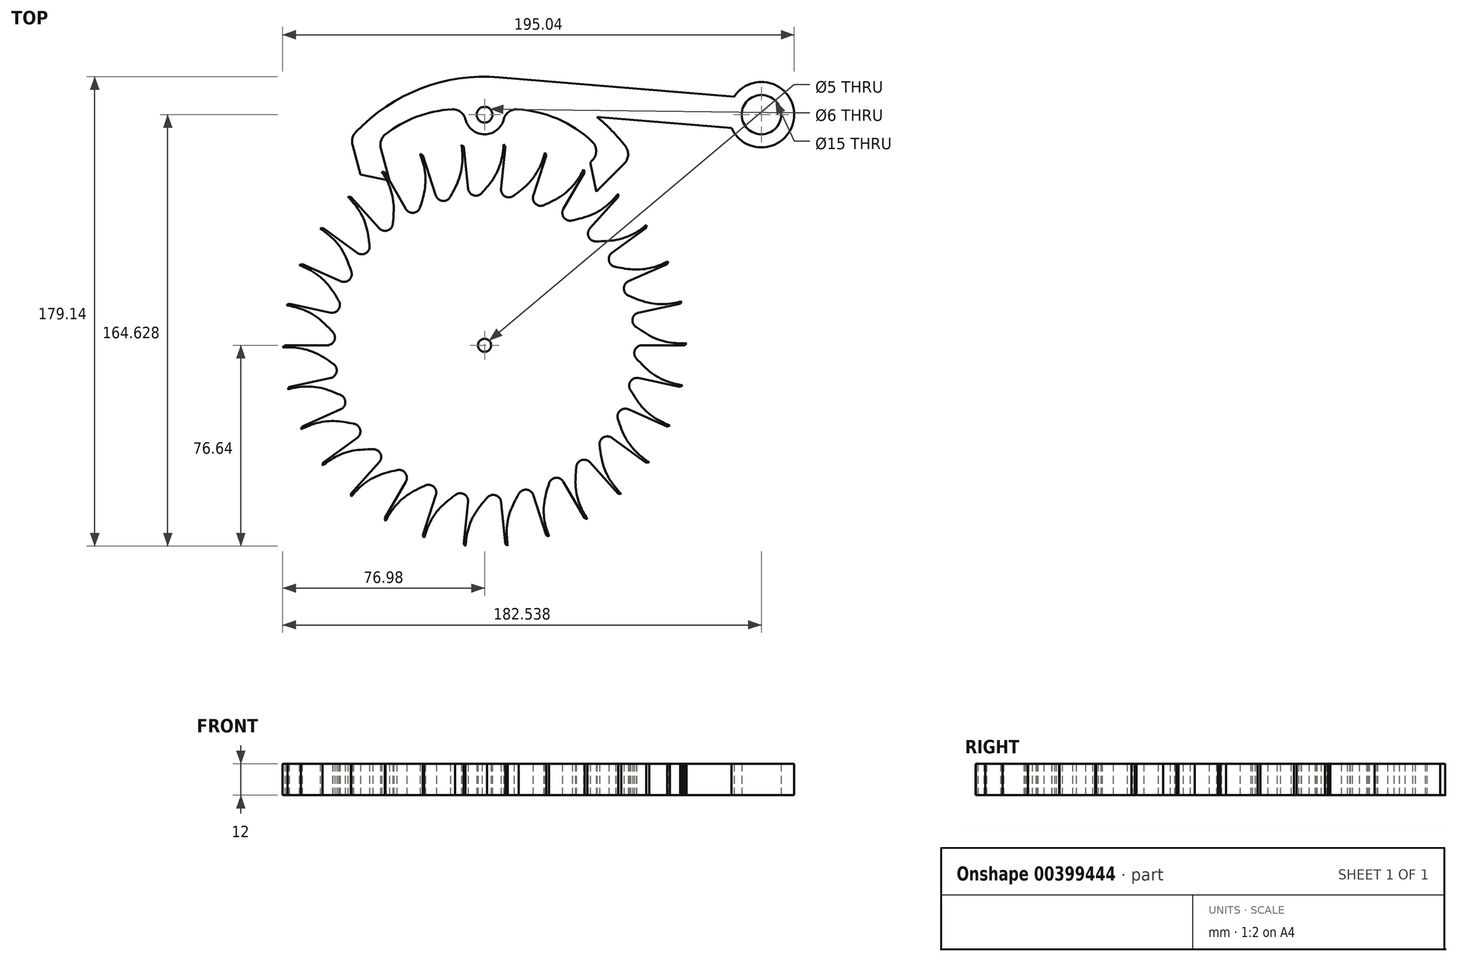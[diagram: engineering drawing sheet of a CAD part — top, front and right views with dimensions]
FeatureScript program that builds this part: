
annotation { "Feature Type Name" : "Feature", "Feature Type Description" : "" }
export const myFeature = defineFeature(function(context is Context, id is Id, definition is map)
    precondition{}
    {
        {
            var Q0;
            Q0=qCreatedBy(makeId("Top.planeOp"),FACE);
            var sketch = newSketch(context, id + "F0", { "sketchPlane" : qUnion([Q0])});
            skCircle(sketch, "E0", {"center": v(0, 0) * mm, "radius": 76.2 * mm, "construction": true});
            skCircle(sketch, "E1", {"center": v(0, 0) * mm, "radius": 95.25 * mm, "construction": true});
            skCircle(sketch, "E2", {"center": v(0, 0) * mm, "radius": 57.15 * mm, "construction": true});
            skLineSegment(sketch, "E3", {"start": v(0, 0) * mm, "end": v(0, 0) * mm});
            skPoint(sketch, "E4.positionSnap0", {"position": v(0, -4366.16) * mm});
            skCircle(sketch, "E5", {"center": v(0, 0) * mm, "radius": 2.5 * mm});
            skLineSegment(sketch, "E6", {"start": v(0, 0) * mm, "end": v(62.62, 108.46) * mm, "construction": true});
            skLineSegment(sketch, "E7", {"start": v(0, 0) * mm, "end": v(-66.51, 115.2) * mm, "construction": true});
            skLineSegment(sketch, "E8", {"start": v(0, 0) * mm, "end": v(-92.02, 102.2) * mm, "construction": true});
            skLineSegment(sketch, "E9", {"start": v(-109.9, 24.54) * mm, "end": v(65, 125.52) * mm, "construction": true});
            skPoint(sketch, "E10", {"position": v(-38.1, 66) * mm});
            skPoint(sketch, "E11", {"position": v(0, 87.99) * mm});
            skLineSegment(sketch, "E12", {"start": v(-101.63, 31.65) * mm, "end": v(76.72, 130.52) * mm, "construction": true});
            skLineSegment(sketch, "E13", {"start": v(-38.1, 66) * mm, "end": v(-39.17, 66.28) * mm});
            skLineSegment(sketch, "E14", {"start": v(-38.1, 66) * mm, "end": v(-28.57, 49.5) * mm});
            skArc(sketch, "E15", {"start": v(-40.2, 44.64) * mm, "mid": v(-36.93, 43.84) * mm, "end": v(-34.97, 46.57) * mm});
            skFitSpline(sketch, "E16", {"points": [v(-39.17, 66.28) * mm, v(-34.97, 46.57) * mm], "startDerivative": vector(5.47, -16.79) * mm, "endDerivative": vector(-0.66, -22.87) * mm});
            skPoint(sketch, "E17", {"position": v(-40.2, 44.64) * mm});
            skSolve(sketch);
        }
        {
            var Q0;
            Q0=qCreatedBy(makeId("Top.planeOp"),FACE);
            var sketch = newSketch(context, id + "F1", { "sketchPlane" : qUnion([Q0])});
            skArc(sketch, "E18.0", {"start": v(-40.2, 44.64) * mm, "mid": v(-36.93, 43.84) * mm, "end": v(-34.97, 46.57) * mm});
            skFitSpline(sketch, "E18.1", {"points": [v(-39.17, 66.28) * mm, v(-36.46, 61.15) * mm, v(-34.75, 54.19) * mm, v(-34.97, 46.57) * mm]});
            skLineSegment(sketch, "E18.2", {"start": v(-38.1, 66) * mm, "end": v(-28.57, 49.5) * mm});
            skLineSegment(sketch, "E19.0", {"start": v(-38.24, 42.47) * mm, "end": v(-40.2, 44.64) * mm});
            skPoint(sketch, "E20.orphan", {"position": v(-92.02, 102.2) * mm});
            skArc(sketch, "E21.0", {"start": v(-38.24, 42.47) * mm, "mid": v(33.6, -46.24) * mm, "end": v(-28.57, 49.5) * mm});
            skCircle(sketch, "E22.1", {"center": v(0, 0) * mm, "radius": 2.5 * mm});
            skLineSegment(sketch, "E23.0", {"start": v(-38.1, 66) * mm, "end": v(-39.17, 66.28) * mm});
            skSolve(sketch);
        }
        {
            var Q0;
            Q0 = qSketchRegion(id + "F1", true);
            extrude(context, id + "F2", {"entities" : qUnion([Q0]), "depth" : 12 * mm});
        }
        {
            var Q0;
            Q0=makeQuery(id+"F2.opExtrude","SWEPT_BODY",BODY,{"disambiguationData":[OSD([sQuery(id+"F1.wireOp",EDGE,"E18.0"),sQuery(id+"F1.wireOp",EDGE,"E18.1"),sQuery(id+"F1.wireOp",EDGE,"E18.2"),sQuery(id+"F1.wireOp",EDGE,"E19.0"),sQuery(id+"F1.wireOp",EDGE,"E21.0"),sQuery(id+"F1.wireOp",EDGE,"E22.1"),sQuery(id+"F1.wireOp",EDGE,"E23.0")])]});
            var Q1;
            Q1=makeQuery(id+"F2.opExtrude","SWEPT_FACE",FACE,{"disambiguationData":[OSD([sQuery(id+"F1.wireOp",EDGE,"E22.1")])]});
            circularPattern(context, id + "F3", {"operationType" : NewBodyOperationType.ADD, "entities" : qUnion([Q0]), "axis" : qUnion([Q1]), "angle" : 360 * degree, "instanceCount" : 30, "equalSpace" : true});
        }
        {
            var Q0;
            Q0=qCreatedBy(makeId("Top.planeOp"),FACE);
            var sketch = newSketch(context, id + "F4", { "sketchPlane" : qUnion([Q0])});
            skLineSegment(sketch, "E24", {"start": v(0, 0) * mm, "end": v(-58.34, 89.84) * mm, "construction": true});
            skLineSegment(sketch, "E25", {"start": v(0, 0) * mm, "end": v(-62.87, 86.53) * mm, "construction": true});
            skLineSegment(sketch, "E26", {"start": v(0, 0) * mm, "end": v(63.2, 97.32) * mm, "construction": true});
            skLineSegment(sketch, "E27", {"start": v(0, 0) * mm, "end": v(67.16, 92.44) * mm, "construction": true});
            skPoint(sketch, "E28", {"position": v(-41.5, 63.9) * mm});
            skPoint(sketch, "E29", {"position": v(41.5, 63.9) * mm});
            skLineSegment(sketch, "E30", {"start": v(-47.33, 65.15) * mm, "end": v(-36.25, 62.8) * mm});
            skLineSegment(sketch, "E31", {"start": v(40.26, 69.74) * mm, "end": v(42.62, 58.66) * mm});
            skLineSegment(sketch, "E32", {"start": v(40.26, 69.74) * mm, "end": v(41.08, 70.56) * mm});
            skLineSegment(sketch, "E33", {"start": v(-36.25, 62.8) * mm, "end": v(-39.58, 75.22) * mm});
            skCircle(sketch, "E34", {"center": v(0, 87.99) * mm, "radius": 3 * mm});
            skArc(sketch, "E35", {"start": v(-7.29, 86.22) * mm, "mid": v(0, 80.49) * mm, "end": v(7.29, 86.22) * mm});
            skArc(sketch, "E36", {"start": v(53.72, 75.88) * mm, "mid": v(3.5, 102.4) * mm, "end": v(-49.19, 81.22) * mm});
            skArc(sketch, "E37.trimOffspring", {"start": v(41, 77.72) * mm, "mid": v(27.8, 86.42) * mm, "end": v(12.41, 90.03) * mm});
            skArc(sketch, "E38.trimOffspring", {"start": v(-12.41, 90.03) * mm, "mid": v(-25.87, 87.2) * mm, "end": v(-37.85, 80.44) * mm});
            skPoint(sketch, "E39.visualSharp", {"position": v(7.22, 90) * mm});
            skArc(sketch, "E39.filletArc", {"start": v(12.41, 90.03) * mm, "mid": v(9.16, 89.05) * mm, "end": v(7.29, 86.22) * mm});
            skPoint(sketch, "E40.visualSharp", {"position": v(-7.22, 90) * mm});
            skArc(sketch, "E40.filletArc", {"start": v(-7.29, 86.22) * mm, "mid": v(-9.16, 89.05) * mm, "end": v(-12.41, 90.03) * mm});
            skLineSegment(sketch, "E41", {"start": v(-47.33, 65.15) * mm, "end": v(-50.38, 76.5) * mm});
            skLineSegment(sketch, "E42", {"start": v(42.62, 58.66) * mm, "end": v(53.27, 69.31) * mm});
            skArc(sketch, "E43.filletArc", {"start": v(-49.19, 81.22) * mm, "mid": v(-50.4, 79.02) * mm, "end": v(-50.38, 76.5) * mm});
            skPoint(sketch, "E44.visualSharp", {"position": v(56.26, 72.3) * mm});
            skArc(sketch, "E44.filletArc", {"start": v(53.27, 69.31) * mm, "mid": v(54.73, 72.51) * mm, "end": v(53.72, 75.88) * mm});
            skPoint(sketch, "E45.visualSharp", {"position": v(-40.4, 78.27) * mm});
            skArc(sketch, "E45.filletArc", {"start": v(-37.85, 80.44) * mm, "mid": v(-39.5, 78.1) * mm, "end": v(-39.58, 75.22) * mm});
            skPoint(sketch, "E46.visualSharp", {"position": v(44.5, 73.98) * mm});
            skArc(sketch, "E46.filletArc", {"start": v(41.08, 70.56) * mm, "mid": v(42.55, 74.16) * mm, "end": v(41, 77.72) * mm});
            skSolve(sketch);
        }
        {
            var Q0;
            Q0 = qSketchRegion(id + "F4", true);
            extrude(context, id + "F5", {"entities" : qUnion([Q0]), "depth" : 12 * mm});
        }
        {
            var Q0;
            Q0=qCreatedBy(makeId("Top.planeOp"),FACE);
            var sketch = newSketch(context, id + "F6", { "sketchPlane" : qUnion([Q0])});
            skLineSegment(sketch, "E47", {"start": v(5.56, 102.27) * mm, "end": v(95.12, 94.87) * mm});
            skCircle(sketch, "E48", {"center": v(105.56, 87.99) * mm, "radius": 7.5 * mm});
            skArc(sketch, "E49", {"start": v(94.14, 82.91) * mm, "mid": v(118.02, 86.96) * mm, "end": v(95.12, 94.87) * mm});
            skLineSegment(sketch, "E50", {"start": v(42.86, 87.15) * mm, "end": v(94.14, 82.91) * mm});
            skLineSegment(sketch, "E51", {"start": v(-30.06, 99.2) * mm, "end": v(126.14, 86.29) * mm, "construction": true});
            skArc(sketch, "E52.0", {"start": v(42.86, 87.15) * mm, "mid": v(25.36, 97.55) * mm, "end": v(5.56, 102.27) * mm});
            skPoint(sketch, "E53.trimOffspring.end.orphan", {"position": v(-49.19, 81.22) * mm});
            skPoint(sketch, "E54.orphan", {"position": v(53.72, 75.88) * mm});
            skPoint(sketch, "E55", {"position": v(0, 87.99) * mm});
            skLineSegment(sketch, "E56", {"start": v(0, 87.99) * mm, "end": v(105.56, 87.99) * mm, "construction": true});
            skSolve(sketch);
        }
        {
            var Q0;
            Q0 = qSketchRegion(id + "F6", true);
            extrude(context, id + "F7", {"entities" : qUnion([Q0]), "operationType" : NewBodyOperationType.ADD, "depth" : 12 * mm});
        }
    });
